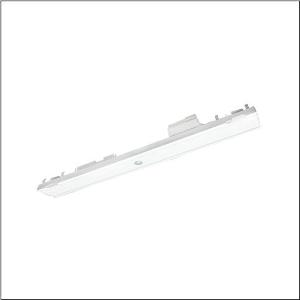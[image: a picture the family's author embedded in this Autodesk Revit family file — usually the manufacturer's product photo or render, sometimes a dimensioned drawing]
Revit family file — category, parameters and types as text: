
# Revit family: licross_r_56tl1e7c4x31_1f0a
name_source: partatom
category: Lighting Fixtures
units: mm (PartAtom-declared; Revit-internal decimal feet)

## family parameters
Cut with Voids When Loaded = No
Host = Face
Light Source = No
Part Type = Normal
Room Calculation Point = No
Round Connector Dimension = Use Diameter
Shared = No

## types (1)
- Licross® (1 x LED, 320 lm, 3.9 W, 4000K)
    Apparent Load = 4 VA
    CIE Flux Codes = 63 91 97 100 100
    Color Rendering = 70
    Color Temperature = 4000K
    Default Elevation = 1800 mm
    Description = Licross®, luminaire insert, of sheet steel, coil coated, white, length: 500mm, width: 59mm, height: 60mm, mounting height: 7..17m, emergency light element,LED rated luminous flux: 320lm, light colour: 740, control gear: CEAG, with plug, 6-pole, with phase selection, mains connection: 220..240V, AC/DC, 0/50..60Hz, rated input power: 3.9W, halogen-free wiring, for trunking rail, 9..14-pole, for emergency light function, supply monitoring module CEAG, with address switch, choice between two emergency light lines via tool-free moving of contact pin prior to installation in trunking rail, primary light control with lens, of PMMA, primary optical cover: cover, of PMMA, light emission: direct distribution, primary light characteristic: asymmetric,  for escape and rescue routes, compatible with all CEAG STAR technology systems (ZB-S, DG-S (DualGuard-S), LP-STAR, AT-S+), protection rating (complete): IP40, insulation class (complete): insulation class I (protective earthing), certification: CE, UKCA, protection symbol: D if used in an environment without relevant dust loads, impact resistance: IK06, permissible ambient temperature for indoor applications: -20..+40°C, packaging unit: 1 piece
    Height = 60 mm  [stored 0.19685 ft]
    Lamp = 1 x LED
    Lamp Light Flux = 320 lm
    Lamp Power = 3.9 W
    Lamp count = 1
    Length = 500 mm
    Luminous efficacy = 82 lm/W
    Manufacturer = Siteco
    ModVariant = No
    Model = 56TL1E7C4X31
    Mounting Place = Ceiling
    Mounting Type = Pendant
    Number of Poles = 1
    OnlyDefault = Yes
    Power Factor = 1
    Product Name = Licross®
    Product group = luminaire insert
    ProductGroupID = 901
    Protection Class = Protection class I
    Protection Degree = IP 40
    RLX_Detail_Level = 1
    RLX_Emergency_Light_Flux = 0 lm
    RLX_Emergency_Type = 0
    RLX_Emergency_Type_DB = No
    RlxData = <blob elided: 31105 chars, md5=e0908137>
    Socket = socket
    Standby Power = 0 W
    System Light Flux = 320 lm
    System Power = 4 W
    Type Comments = Product without accessories
    Type Image = l_1251804.jpg
    URL = http://relux.com
    VarID = ---
    Voltage = 0 V
    Weight = 0.00 kg
    Width = 59 mm

note: [stored X ft] marks values corroborated as IEEE doubles in the binary element streams (Revit-internal decimal feet)

## geometry (parser evidence)
native form markers: Blend x4, Sweep x8
no freeform markers — native parametric forms only
